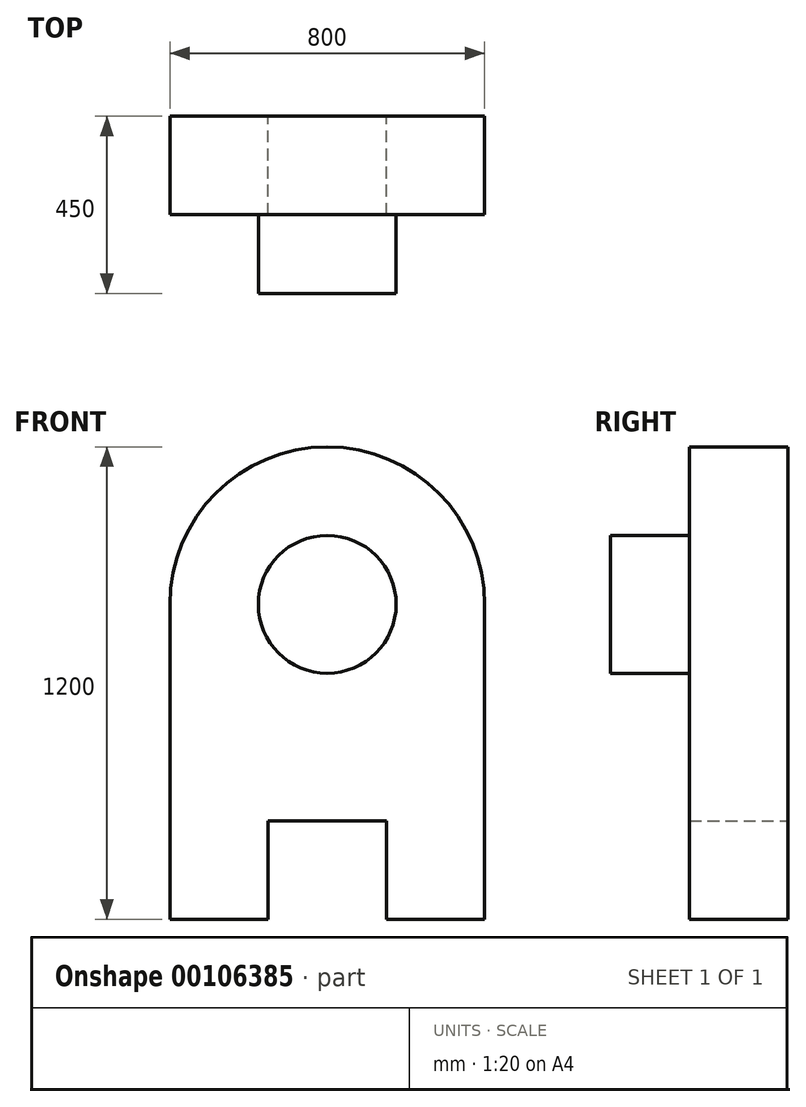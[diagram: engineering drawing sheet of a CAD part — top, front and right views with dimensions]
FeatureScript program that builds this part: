
annotation { "Feature Type Name" : "Feature", "Feature Type Description" : "" }
export const myFeature = defineFeature(function(context is Context, id is Id, definition is map)
    precondition{}
    {
        {
            var Q0;
            Q0=qCreatedBy(makeId("Front.planeOp"),FACE);
            var sketch = newSketch(context, id + "F0", { "sketchPlane" : qUnion([Q0])});
            skLineSegment(sketch, "E0.top", {"start": v(400, -400) * mm, "end": v(150, -400) * mm});
            skLineSegment(sketch, "E0.left", {"start": v(400, 400) * mm, "end": v(400, -400) * mm});
            skLineSegment(sketch, "E0.right", {"start": v(-400, 400) * mm, "end": v(-400, -400) * mm});
            skPoint(sketch, "E0.middle", {"position": v(0, 0) * mm});
            skArc(sketch, "E1", {"start": v(400, 400) * mm, "mid": v(0, 800) * mm, "end": v(-400, 400) * mm});
            skLineSegment(sketch, "E2.bottom", {"start": v(150, -150) * mm, "end": v(-150, -150) * mm});
            skLineSegment(sketch, "E2.left", {"start": v(150, -150) * mm, "end": v(150, -400) * mm});
            skLineSegment(sketch, "E2.right", {"start": v(-150, -150) * mm, "end": v(-150, -400) * mm});
            skPoint(sketch, "E2.middle", {"position": v(0, -400) * mm});
            skPoint(sketch, "E3.orphan", {"position": v(-150, -650) * mm});
            skPoint(sketch, "E4.orphan", {"position": v(150, -650) * mm});
            skLineSegment(sketch, "E5.trimOffspring", {"start": v(-150, -400) * mm, "end": v(-400, -400) * mm});
            skSolve(sketch);
        }
        {
            var Q0;
            Q0 = qSketchRegion(id + "F0", true);
            extrude(context, id + "F1", {"entities" : qUnion([Q0]), "depth" : 250 * mm});
        }
        {
            var Q0;
            Q0=makeQuery(id+"F1.opExtrude","CAP_FACE",FACE,{"disambiguationData":[OSD([sQuery(id+"F0.wireOp",EDGE,"E0.top"),sQuery(id+"F0.wireOp",EDGE,"E0.left"),sQuery(id+"F0.wireOp",EDGE,"E0.right"),sQuery(id+"F0.wireOp",EDGE,"E1"),sQuery(id+"F0.wireOp",EDGE,"E2.bottom"),sQuery(id+"F0.wireOp",EDGE,"E2.left"),sQuery(id+"F0.wireOp",EDGE,"E2.right"),sQuery(id+"F0.wireOp",EDGE,"E5.trimOffspring")])],"isStart":false});
            var sketch = newSketch(context, id + "F2", { "sketchPlane" : qUnion([Q0])});
            skCircle(sketch, "E6", {"center": v(0, 400) * mm, "radius": 175 * mm});
            skSolve(sketch);
        }
        {
            var Q0;
            Q0 = qSketchRegion(id + "F2", true);
            extrude(context, id + "F3", {"entities" : qUnion([Q0]), "operationType" : NewBodyOperationType.ADD, "depth" : 200 * mm});
        }
    });
